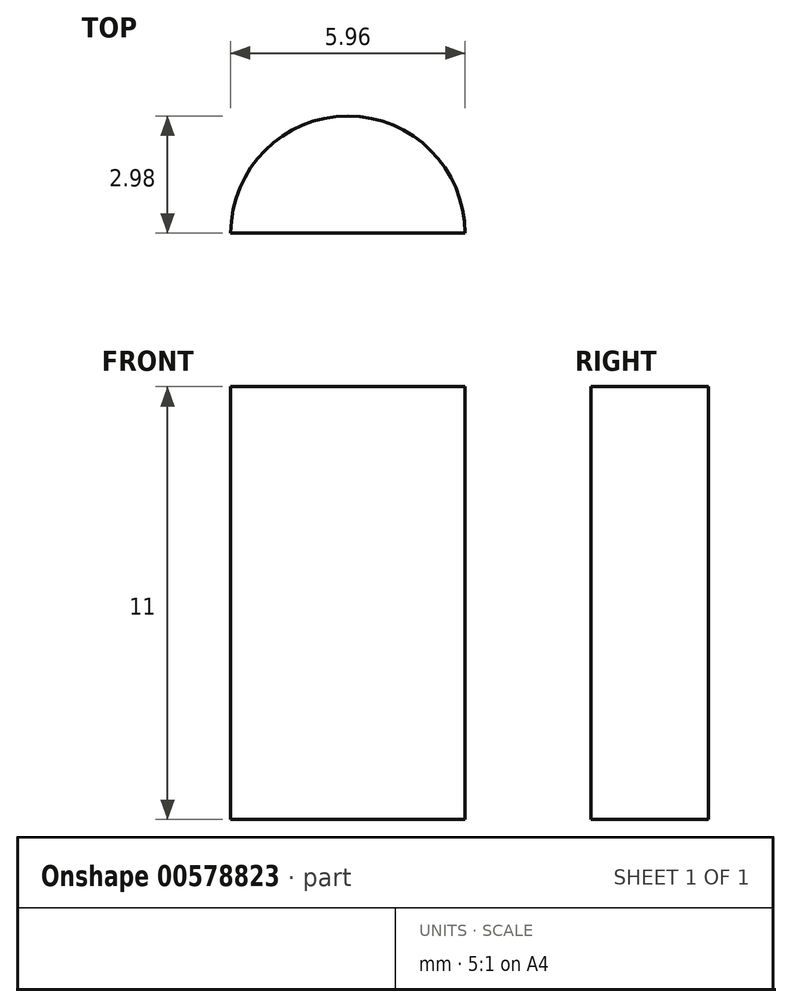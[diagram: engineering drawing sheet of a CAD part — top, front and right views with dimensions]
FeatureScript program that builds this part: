
annotation { "Feature Type Name" : "Feature", "Feature Type Description" : "" }
export const myFeature = defineFeature(function(context is Context, id is Id, definition is map)
    precondition{}
    {
        {
            var Q0;
            Q0=qCreatedBy(makeId("Top.planeOp"),FACE);
            var sketch = newSketch(context, id + "F0", { "sketchPlane" : qUnion([Q0])});
            skCircle(sketch, "E0", {"center": v(0, 0) * mm, "radius": 2.98 * mm});
            skLineSegment(sketch, "E1", {"start": v(-2.98, 0) * mm, "end": v(2.98, 0) * mm});
            skSolve(sketch);
        }
        {
            var Q0;
            {var subQ0=sQuery(id+"F0.wireOp",EDGE,"E1");Q0=makeQuery(id+"F0.imprint","IMPRINT",FACE,{"disambiguationData":[TD([[makeQuery(id+"F0.imprint","IMPRINT",EDGE,{"derivedFrom":subQ0}),1.0]])]});}
            extrude(context, id + "F1", {"entities" : qUnion([Q0]), "depth" : 11 * mm, "offsetDistance" : 25 * mm});
        }
    });
